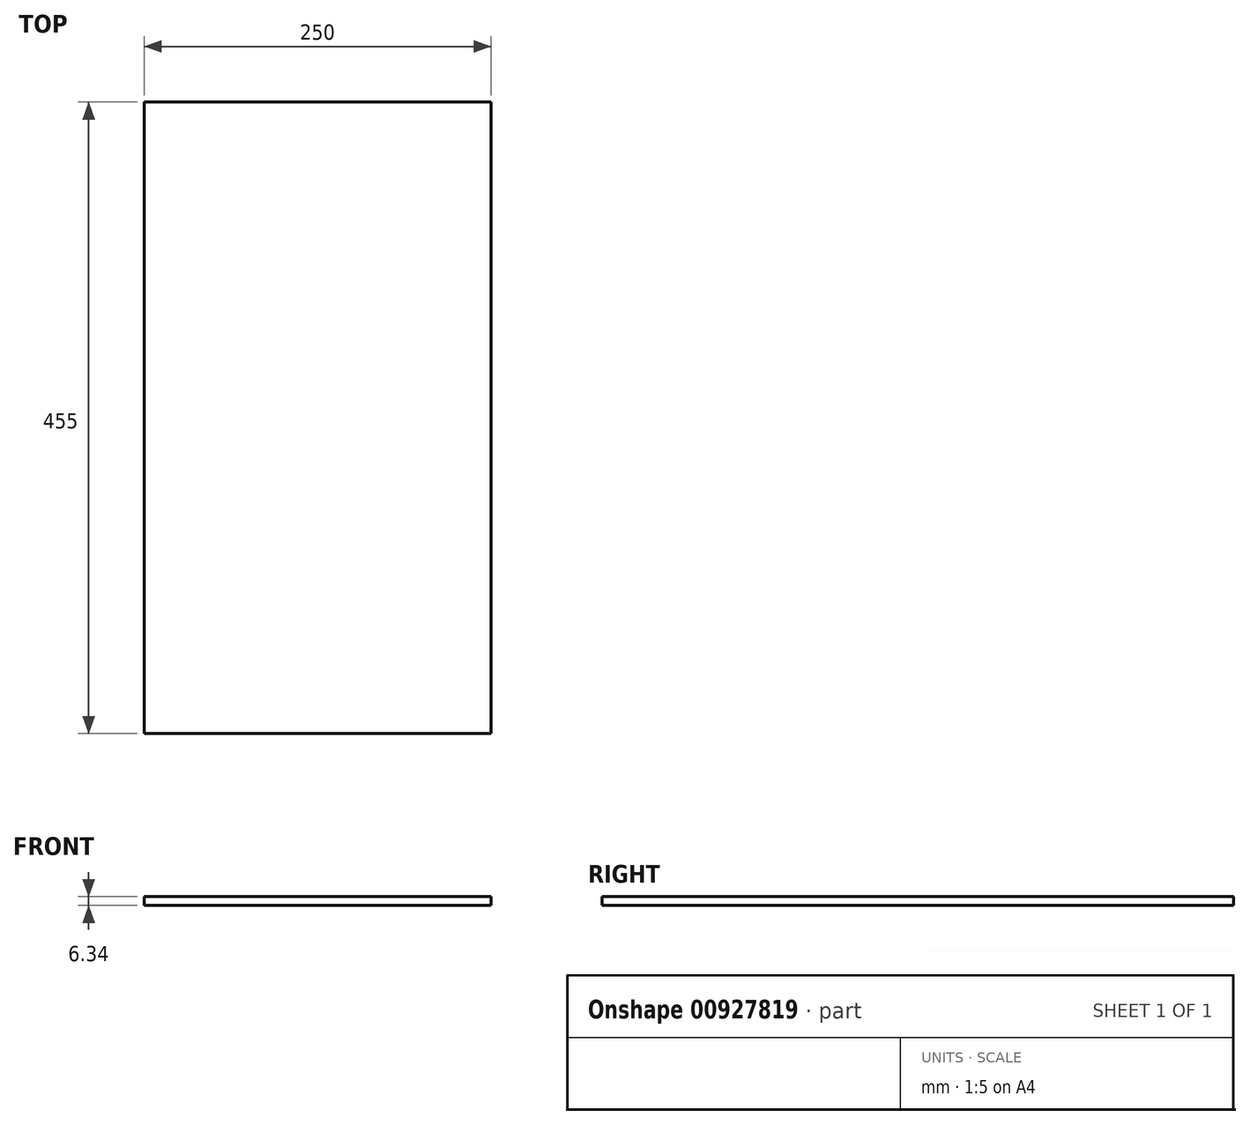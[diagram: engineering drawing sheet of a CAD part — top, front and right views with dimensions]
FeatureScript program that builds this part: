
annotation { "Feature Type Name" : "Feature", "Feature Type Description" : "" }
export const myFeature = defineFeature(function(context is Context, id is Id, definition is map)
    precondition{}
    {
        {
            var Q0;
            Q0=qCreatedBy(makeId("Front.planeOp"),FACE);
            var sketch = newSketch(context, id + "F0", { "sketchPlane" : qUnion([Q0])});
            skLineSegment(sketch, "E0.bottom", {"start": v(125, 3.17) * mm, "end": v(-125, 3.17) * mm});
            skLineSegment(sketch, "E0.top", {"start": v(125, -3.17) * mm, "end": v(-125, -3.17) * mm});
            skLineSegment(sketch, "E0.left", {"start": v(125, 3.18) * mm, "end": v(125, -3.18) * mm});
            skLineSegment(sketch, "E0.right", {"start": v(-125, 3.18) * mm, "end": v(-125, -3.18) * mm});
            skPoint(sketch, "E0.middle", {"position": v(0, 0) * mm});
            skSolve(sketch);
        }
        {
            var Q0;
            Q0=qSketchRegion(id+"F0",true);
            extrude(context, id + "F1", {"entities" : qUnion([Q0]), "depth" : 455 * mm, "offsetDistance" : 25 * mm});
        }
    });
